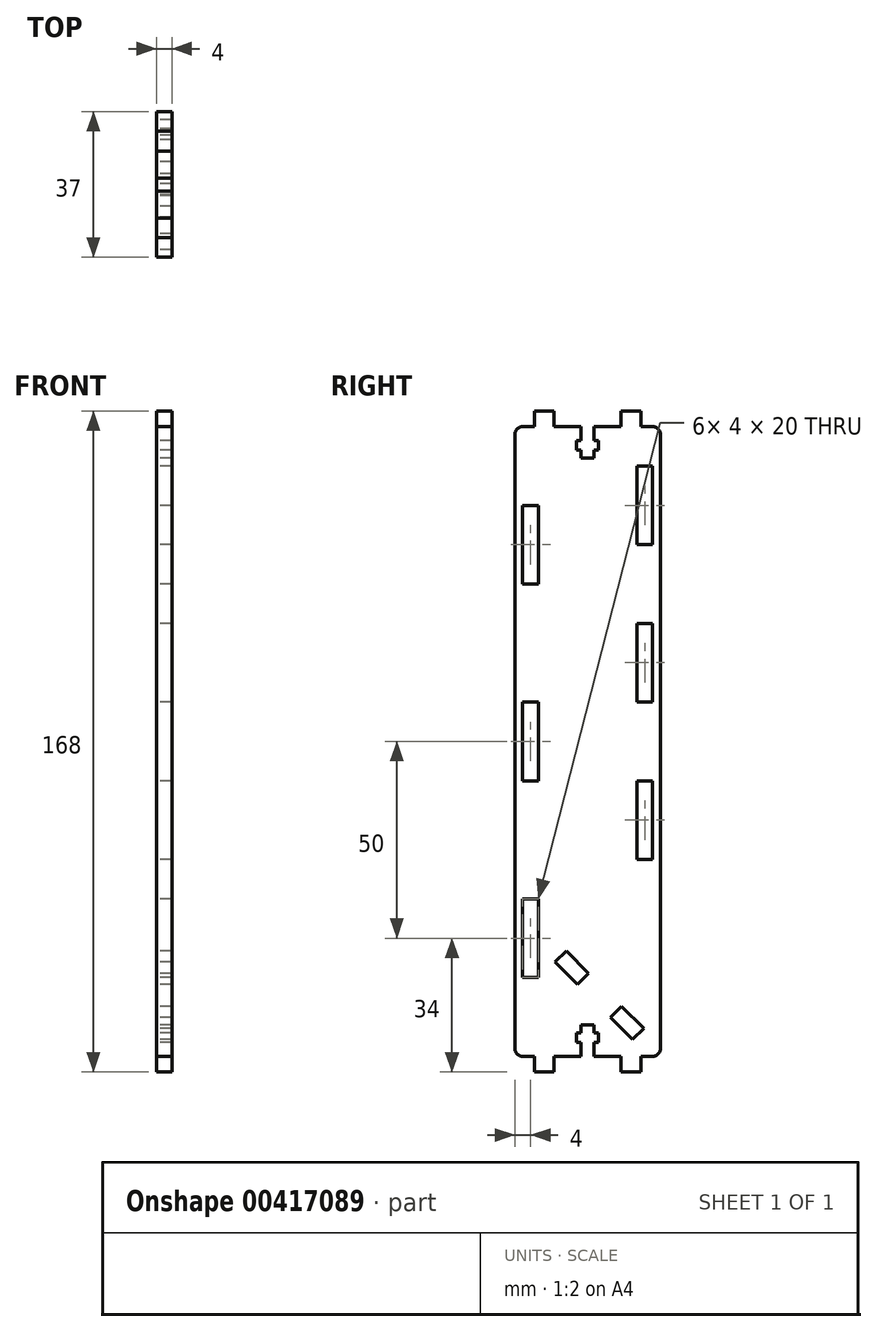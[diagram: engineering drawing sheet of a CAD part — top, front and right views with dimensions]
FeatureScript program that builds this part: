
annotation { "Feature Type Name" : "Feature", "Feature Type Description" : "" }
export const myFeature = defineFeature(function(context is Context, id is Id, definition is map)
    precondition{}
    {
        {
            var Q0;
            Q0=qCreatedBy(makeId("Right.planeOp"),FACE);
            var sketch = newSketch(context, id + "F0", { "sketchPlane" : qUnion([Q0])});
            skLineSegment(sketch, "E0.bottom", {"start": v(18.5, -80) * mm, "end": v(13.5, -80) * mm});
            skLineSegment(sketch, "E0.top", {"start": v(18.5, 80) * mm, "end": v(13.5, 80) * mm});
            skLineSegment(sketch, "E0.left", {"start": v(18.5, -80) * mm, "end": v(18.5, 80) * mm});
            skLineSegment(sketch, "E0.right", {"start": v(-18.5, -80) * mm, "end": v(-18.5, 80) * mm});
            skPoint(sketch, "E0.middle", {"position": v(0, 0) * mm});
            skLineSegment(sketch, "E1.bottom", {"start": v(-16.5, 60) * mm, "end": v(-12.5, 60) * mm});
            skLineSegment(sketch, "E1.top", {"start": v(-16.5, 40) * mm, "end": v(-12.5, 40) * mm});
            skLineSegment(sketch, "E1.left", {"start": v(-16.5, 60) * mm, "end": v(-16.5, 40) * mm});
            skLineSegment(sketch, "E1.right", {"start": v(-12.5, 60) * mm, "end": v(-12.5, 40) * mm});
            skLineSegment(sketch, "E2.bottom", {"start": v(-16.5, 0) * mm, "end": v(-12.5, 0) * mm});
            skLineSegment(sketch, "E2.top", {"start": v(-16.5, 10) * mm, "end": v(-12.5, 10) * mm});
            skLineSegment(sketch, "E2.left", {"start": v(-16.5, 0) * mm, "end": v(-16.5, 10) * mm});
            skLineSegment(sketch, "E2.right", {"start": v(-12.5, 0) * mm, "end": v(-12.5, 10) * mm});
            skLineSegment(sketch, "E3.MirrorCS", {"start": v(-16.5, -40) * mm, "end": v(-12.5, -40) * mm});
            skLineSegment(sketch, "E4.MirrorCS", {"start": v(-16.5, -10) * mm, "end": v(-12.5, -10) * mm});
            skLineSegment(sketch, "E5.MirrorCS", {"start": v(-16.5, 0) * mm, "end": v(-16.5, -10) * mm});
            skLineSegment(sketch, "E6.MirrorCS", {"start": v(-12.5, 0) * mm, "end": v(-12.5, -10) * mm});
            skLineSegment(sketch, "E7.MirrorCS", {"start": v(-12.5, -60) * mm, "end": v(-12.5, -40) * mm});
            skLineSegment(sketch, "E8.MirrorCS", {"start": v(-16.5, -60) * mm, "end": v(-16.5, -40) * mm});
            skLineSegment(sketch, "E9.MirrorCS", {"start": v(-16.5, -60) * mm, "end": v(-12.5, -60) * mm});
            skLineSegment(sketch, "E10", {"start": v(-18.5, 20) * mm, "end": v(18.5, 20) * mm, "construction": true});
            skLineSegment(sketch, "E11.bottom", {"start": v(12.5, 70) * mm, "end": v(16.5, 70) * mm});
            skLineSegment(sketch, "E11.top", {"start": v(12.5, 50) * mm, "end": v(16.5, 50) * mm});
            skLineSegment(sketch, "E11.left", {"start": v(12.5, 70) * mm, "end": v(12.5, 50) * mm});
            skLineSegment(sketch, "E11.right", {"start": v(16.5, 70) * mm, "end": v(16.5, 50) * mm});
            skLineSegment(sketch, "E12.bottom", {"start": v(12.5, 20) * mm, "end": v(16.5, 20) * mm});
            skLineSegment(sketch, "E12.top", {"start": v(12.5, 30) * mm, "end": v(16.5, 30) * mm});
            skLineSegment(sketch, "E12.left", {"start": v(12.5, 20) * mm, "end": v(12.5, 30) * mm});
            skLineSegment(sketch, "E12.right", {"start": v(16.5, 20) * mm, "end": v(16.5, 30) * mm});
            skLineSegment(sketch, "E13.MirrorCS", {"start": v(12.5, -10) * mm, "end": v(16.5, -10) * mm});
            skLineSegment(sketch, "E14.MirrorCS", {"start": v(12.5, 10) * mm, "end": v(16.5, 10) * mm});
            skLineSegment(sketch, "E15.MirrorCS", {"start": v(12.5, -30) * mm, "end": v(16.5, -30) * mm});
            skLineSegment(sketch, "E16.MirrorCS", {"start": v(12.5, -30) * mm, "end": v(12.5, -10) * mm});
            skLineSegment(sketch, "E17.MirrorCS", {"start": v(16.5, 20) * mm, "end": v(16.5, 10) * mm});
            skLineSegment(sketch, "E18.MirrorCS", {"start": v(12.5, 20) * mm, "end": v(12.5, 10) * mm});
            skLineSegment(sketch, "E19.MirrorCS", {"start": v(16.5, -30) * mm, "end": v(16.5, -10) * mm});
            skLineSegment(sketch, "E20", {"start": v(18.5, -80) * mm, "end": v(-12.5, -49) * mm, "construction": true});
            skLineSegment(sketch, "E21", {"start": v(-6.84, -54.66) * mm, "end": v(-5.43, -53.24) * mm});
            skLineSegment(sketch, "E22", {"start": v(-5.43, -53.24) * mm, "end": v(0.23, -58.9) * mm});
            skLineSegment(sketch, "E23", {"start": v(0.23, -58.9) * mm, "end": v(-1.19, -60.31) * mm});
            skLineSegment(sketch, "E24.MirrorCS", {"start": v(-2.6, -61.73) * mm, "end": v(-1.19, -60.31) * mm});
            skLineSegment(sketch, "E25.MirrorCS", {"start": v(-6.84, -54.66) * mm, "end": v(-8.26, -56.07) * mm});
            skLineSegment(sketch, "E26.MirrorCS", {"start": v(-8.26, -56.07) * mm, "end": v(-2.6, -61.73) * mm});
            skLineSegment(sketch, "E27", {"start": v(3, -64.5) * mm, "end": v(-2.21, -69.71) * mm, "construction": true});
            skLineSegment(sketch, "E28.MirrorCS", {"start": v(12.84, -74.34) * mm, "end": v(14.26, -72.93) * mm});
            skLineSegment(sketch, "E29.MirrorCS", {"start": v(5.77, -70.1) * mm, "end": v(7.19, -68.69) * mm});
            skLineSegment(sketch, "E30.MirrorCS", {"start": v(12.84, -74.34) * mm, "end": v(11.43, -75.76) * mm});
            skLineSegment(sketch, "E31.MirrorCS", {"start": v(8.6, -67.27) * mm, "end": v(7.19, -68.69) * mm});
            skLineSegment(sketch, "E32.MirrorCS", {"start": v(14.26, -72.93) * mm, "end": v(8.6, -67.27) * mm});
            skLineSegment(sketch, "E33.MirrorCS", {"start": v(11.43, -75.76) * mm, "end": v(5.77, -70.1) * mm});
            skLineSegment(sketch, "E34.top", {"start": v(-13.5, -84) * mm, "end": v(-8.5, -84) * mm});
            skLineSegment(sketch, "E34.left", {"start": v(-13.5, -80) * mm, "end": v(-13.5, -84) * mm});
            skLineSegment(sketch, "E34.right", {"start": v(-8.5, -80) * mm, "end": v(-8.5, -84) * mm});
            skLineSegment(sketch, "E35.MirrorCS", {"start": v(13.5, -80) * mm, "end": v(13.5, -84) * mm});
            skLineSegment(sketch, "E36.MirrorCS", {"start": v(13.5, -84) * mm, "end": v(8.5, -84) * mm});
            skLineSegment(sketch, "E37.MirrorCS", {"start": v(8.5, -80) * mm, "end": v(8.5, -84) * mm});
            skLineSegment(sketch, "E38.MirrorCS", {"start": v(13.5, 84) * mm, "end": v(8.5, 84) * mm});
            skLineSegment(sketch, "E39.MirrorCS", {"start": v(18.5, 80) * mm, "end": v(-12.5, 49) * mm, "construction": true});
            skLineSegment(sketch, "E40.MirrorCS", {"start": v(13.5, 80) * mm, "end": v(13.5, 84) * mm});
            skLineSegment(sketch, "E41.MirrorCS", {"start": v(-8.5, 80) * mm, "end": v(-8.5, 84) * mm});
            skLineSegment(sketch, "E42.MirrorCS", {"start": v(-13.5, 84) * mm, "end": v(-8.5, 84) * mm});
            skLineSegment(sketch, "E43.MirrorCS", {"start": v(-13.5, 80) * mm, "end": v(-13.5, 84) * mm});
            skLineSegment(sketch, "E44.MirrorCS", {"start": v(8.5, 80) * mm, "end": v(8.5, 84) * mm});
            skLineSegment(sketch, "E45.trimOffspring", {"start": v(-13.5, -80) * mm, "end": v(-18.5, -80) * mm});
            skLineSegment(sketch, "E46.trimOffspring", {"start": v(8.5, -80) * mm, "end": v(1.65, -80) * mm});
            skLineSegment(sketch, "E47.trimOffspring", {"start": v(-13.5, 80) * mm, "end": v(-18.5, 80) * mm});
            skLineSegment(sketch, "E48.trimOffspring", {"start": v(8.5, 80) * mm, "end": v(1.65, 80) * mm});
            skLineSegment(sketch, "E49.top", {"start": v(1.65, 72) * mm, "end": v(-1.65, 72) * mm});
            skLineSegment(sketch, "E49.left", {"start": v(1.65, 80) * mm, "end": v(1.65, 76.5) * mm});
            skLineSegment(sketch, "E49.right", {"start": v(-1.65, 80) * mm, "end": v(-1.65, 76.5) * mm});
            skPoint(sketch, "E49.middle", {"position": v(0, 76) * mm});
            skLineSegment(sketch, "E50.bottom", {"start": v(2.8, 74) * mm, "end": v(1.65, 74) * mm});
            skLineSegment(sketch, "E50.top", {"start": v(2.8, 76.5) * mm, "end": v(1.65, 76.5) * mm});
            skLineSegment(sketch, "E50.left", {"start": v(2.8, 74) * mm, "end": v(2.8, 76.5) * mm});
            skLineSegment(sketch, "E50.right", {"start": v(-2.8, 74) * mm, "end": v(-2.8, 76.5) * mm});
            skPoint(sketch, "E50.middle", {"position": v(0, 75.25) * mm});
            skLineSegment(sketch, "E51.trimOffspring", {"start": v(-1.65, 76.5) * mm, "end": v(-2.8, 76.5) * mm});
            skLineSegment(sketch, "E52.trimOffspring", {"start": v(-1.65, 74) * mm, "end": v(-1.65, 72) * mm});
            skLineSegment(sketch, "E53.trimOffspring", {"start": v(1.65, 74) * mm, "end": v(1.65, 72) * mm});
            skLineSegment(sketch, "E54.trimOffspring", {"start": v(-1.65, 74) * mm, "end": v(-2.8, 74) * mm});
            skLineSegment(sketch, "E55.trimOffspring", {"start": v(-1.65, 80) * mm, "end": v(-8.5, 80) * mm});
            skLineSegment(sketch, "E56.MirrorCS", {"start": v(-1.65, -76.5) * mm, "end": v(-2.8, -76.5) * mm});
            skPoint(sketch, "E57.MirrorP", {"position": v(0, -75.25) * mm});
            skLineSegment(sketch, "E58.MirrorCS", {"start": v(1.65, -74) * mm, "end": v(1.65, -72) * mm});
            skLineSegment(sketch, "E59.MirrorCS", {"start": v(2.8, -74) * mm, "end": v(2.8, -76.5) * mm});
            skLineSegment(sketch, "E60.MirrorCS", {"start": v(-2.8, -74) * mm, "end": v(-2.8, -76.5) * mm});
            skLineSegment(sketch, "E61.MirrorCS", {"start": v(1.65, -72) * mm, "end": v(-1.65, -72) * mm});
            skPoint(sketch, "E62.MirrorP", {"position": v(0, -76) * mm});
            skLineSegment(sketch, "E63.MirrorCS", {"start": v(2.8, -76.5) * mm, "end": v(1.65, -76.5) * mm});
            skLineSegment(sketch, "E64.MirrorCS", {"start": v(-1.65, -74) * mm, "end": v(-1.65, -72) * mm});
            skLineSegment(sketch, "E65.MirrorCS", {"start": v(-1.65, -80) * mm, "end": v(-1.65, -76.5) * mm});
            skLineSegment(sketch, "E66.MirrorCS", {"start": v(-1.65, -74) * mm, "end": v(-2.8, -74) * mm});
            skLineSegment(sketch, "E67.MirrorCS", {"start": v(2.8, -74) * mm, "end": v(1.65, -74) * mm});
            skLineSegment(sketch, "E68.MirrorCS", {"start": v(1.65, -80) * mm, "end": v(1.65, -76.5) * mm});
            skLineSegment(sketch, "E69.trimOffspring", {"start": v(-1.65, -80) * mm, "end": v(-8.5, -80) * mm});
            skSolve(sketch);
        }
        {
            var Q0;
            Q0=makeQuery(id+"F0.imprint","IMPRINT",FACE,{"disambiguationData":[TD([[makeQuery(id+"F0.imprint","IMPRINT",EDGE,{"derivedFrom":sQuery(id+"F0.wireOp",EDGE,"E0.bottom")}),-1.0]])]});
            extrude(context, id + "F1", {"entities" : qUnion([Q0]), "depth" : 4 * mm});
        }
        {
            var Q0;
            Q0=makeQuery(id+"F1.opExtrude","SWEPT_EDGE",EDGE,{"disambiguationData":[OSD([sQuery(id+"F0.wireOp",EDGE,"E0.right"),sQuery(id+"F0.wireOp",EDGE,"E45.trimOffspring")])]});
            var Q1;
            Q1=makeQuery(id+"F1.opExtrude","SWEPT_EDGE",EDGE,{"disambiguationData":[OSD([sQuery(id+"F0.wireOp",EDGE,"E0.bottom"),sQuery(id+"F0.wireOp",EDGE,"E0.left")])]});
            var Q2;
            Q2=makeQuery(id+"F1.opExtrude","SWEPT_EDGE",EDGE,{"disambiguationData":[OSD([sQuery(id+"F0.wireOp",EDGE,"E0.right"),sQuery(id+"F0.wireOp",EDGE,"E47.trimOffspring")])]});
            var Q3;
            Q3=makeQuery(id+"F1.opExtrude","SWEPT_EDGE",EDGE,{"disambiguationData":[OSD([sQuery(id+"F0.wireOp",EDGE,"E0.left"),sQuery(id+"F0.wireOp",EDGE,"E0.top")])]});
            fillet(context, id + "F2", {"entities" : qUnion([Q0, Q1, Q2, Q3]), "radius" : 2 * mm, "tangentPropagation" : true, "allowEdgeOverflow" : false});
        }
    });
